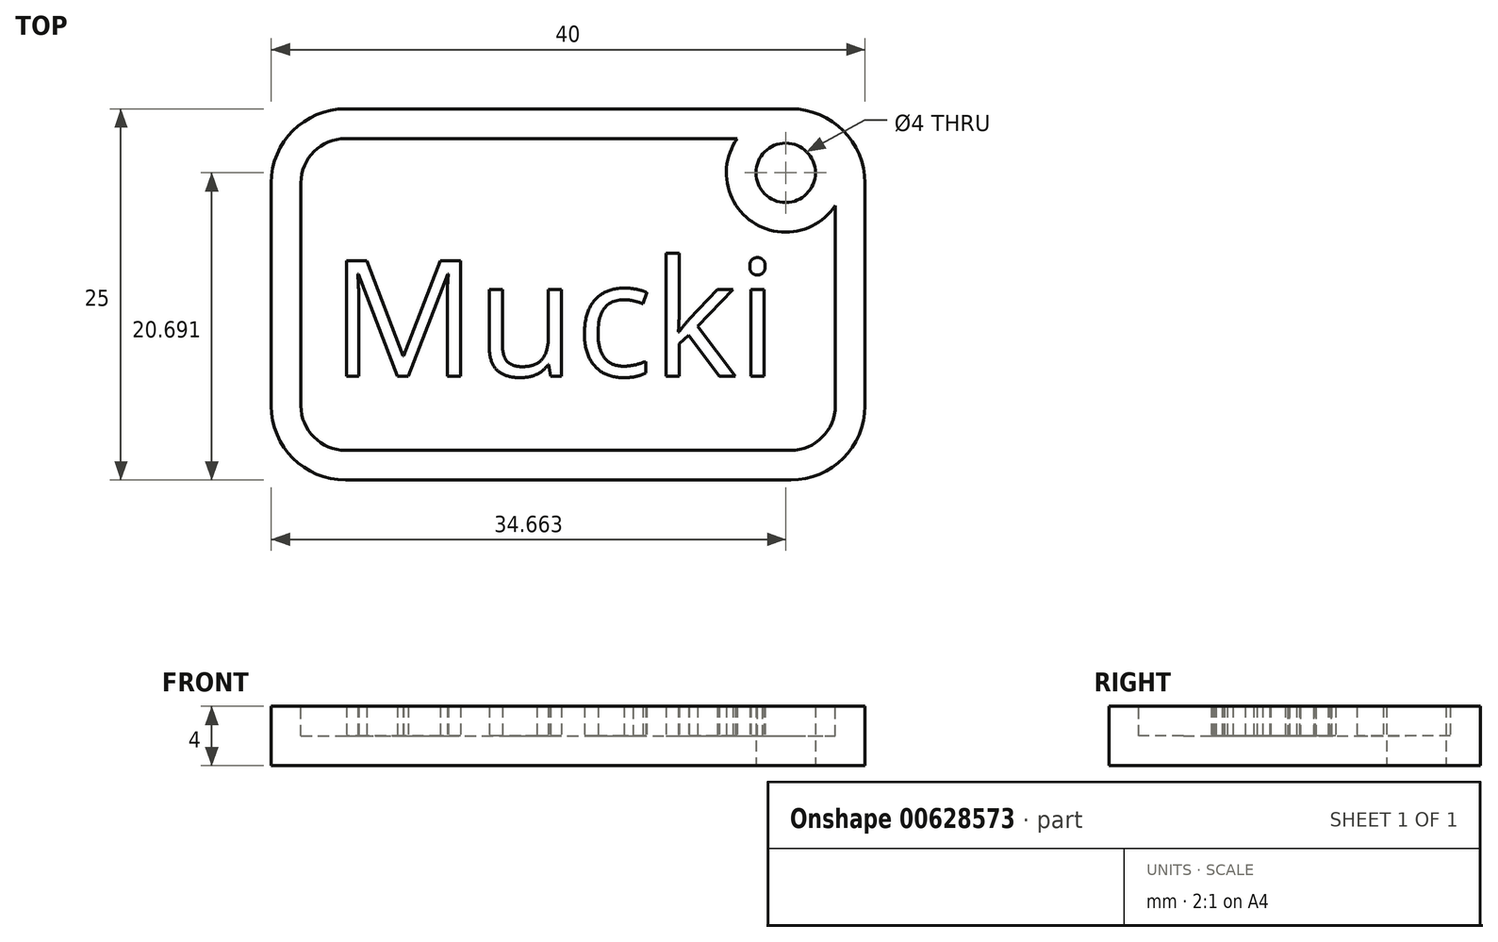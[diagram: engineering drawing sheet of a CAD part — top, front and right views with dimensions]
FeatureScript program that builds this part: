
annotation { "Feature Type Name" : "Feature", "Feature Type Description" : "" }
export const myFeature = defineFeature(function(context is Context, id is Id, definition is map)
    precondition{}
    {
        {
            var Q0;
            Q0=qCreatedBy(makeId("Top.planeOp"),FACE);
            var sketch = newSketch(context, id + "F0", { "sketchPlane" : qUnion([Q0])});
            skLineSegment(sketch, "E0.bottom", {"start": v(5, 0) * mm, "end": v(35, 0) * mm});
            skLineSegment(sketch, "E0.top", {"start": v(5, 25) * mm, "end": v(35, 25) * mm});
            skLineSegment(sketch, "E0.left", {"start": v(0, 5) * mm, "end": v(0, 20) * mm});
            skLineSegment(sketch, "E0.right", {"start": v(40, 5) * mm, "end": v(40, 20) * mm});
            skPoint(sketch, "E1.visualSharp", {"position": v(0, 25) * mm});
            skArc(sketch, "E1.filletArc", {"start": v(5, 25) * mm, "mid": v(1.46, 23.54) * mm, "end": v(0, 20) * mm});
            skPoint(sketch, "E2.visualSharp", {"position": v(0, 0) * mm});
            skArc(sketch, "E2.filletArc", {"start": v(0, 5) * mm, "mid": v(1.46, 1.46) * mm, "end": v(5, 0) * mm});
            skPoint(sketch, "E3.visualSharp", {"position": v(40, 0) * mm});
            skArc(sketch, "E3.filletArc", {"start": v(35, 0) * mm, "mid": v(38.54, 1.46) * mm, "end": v(40, 5) * mm});
            skPoint(sketch, "E4.visualSharp", {"position": v(40, 25) * mm});
            skArc(sketch, "E4.filletArc", {"start": v(40, 20) * mm, "mid": v(38.54, 23.54) * mm, "end": v(35, 25) * mm});
            skSolve(sketch);
        }
        {
            var Q0;
            Q0=qCreatedBy(makeId("Top.planeOp"),FACE);
            var sketch = newSketch(context, id + "F1", { "sketchPlane" : qUnion([Q0])});
            skPoint(sketch, "E5", {"position": v(34.66, 20.7) * mm});
            skSolve(sketch);
        }
        {
            var Q0;
            Q0 = qSketchRegion(id + "F0", true);
            extrude(context, id + "F2", {"entities" : qUnion([Q0]), "depth" : 4 * mm, "offsetDistance" : 25 * mm});
        }
        {
            var Q0;
            Q0=sQuery(id+"F1.wireOp",VERTEX,"E5");
            var Q1;
            Q1=makeQuery(id+"F2.opExtrude","SWEPT_BODY",BODY,{"disambiguationData":[OSD([sQuery(id+"F0.wireOp",EDGE,"E0.bottom"),sQuery(id+"F0.wireOp",EDGE,"E0.top"),sQuery(id+"F0.wireOp",EDGE,"E0.left"),sQuery(id+"F0.wireOp",EDGE,"E0.right"),sQuery(id+"F0.wireOp",EDGE,"E1.filletArc"),sQuery(id+"F0.wireOp",EDGE,"E2.filletArc"),sQuery(id+"F0.wireOp",EDGE,"E3.filletArc"),sQuery(id+"F0.wireOp",EDGE,"E4.filletArc")])]});
            hole(context, id + "F3", {"style" : HoleStyle.SIMPLE, "endStyle" : HoleEndStyle.THROUGH, "oppositeDirection" : true, "holeDiameter" : 4 * mm, "majorDiameter" : 5 * mm, "isTappedThrough" : true, "tappedDepth" : 12 * mm, "tapClearance" : 3, "locations" : qUnion([Q0]), "scope" : qUnion([Q1])});
        }
        {
            var Q0;
            Q0=makeQuery(id+"F2.opExtrude","CAP_FACE",FACE,{"disambiguationData":[OSD([sQuery(id+"F0.wireOp",EDGE,"E0.bottom"),sQuery(id+"F0.wireOp",EDGE,"E0.top"),sQuery(id+"F0.wireOp",EDGE,"E0.left"),sQuery(id+"F0.wireOp",EDGE,"E0.right"),sQuery(id+"F0.wireOp",EDGE,"E1.filletArc"),sQuery(id+"F0.wireOp",EDGE,"E2.filletArc"),sQuery(id+"F0.wireOp",EDGE,"E3.filletArc"),sQuery(id+"F0.wireOp",EDGE,"E4.filletArc")])],"isStart":false});
            shell(context, id + "F4", {"entities" : qUnion([Q0]), "thickness" : 2 * mm});
        }
        {
            var Q0;
            Q0=qCreatedBy(makeId("Top.planeOp"),FACE);
            var sketch = newSketch(context, id + "F5", { "sketchPlane" : qUnion([Q0])});
            skText(sketch, "E6", { "text": "Mucki", "fontName": "OpenSans-Regular.ttf"});
            const initialGuessF5  = {"E6": [0.004, 0.007, 1, 0, 0.00783]};
            skSetInitialGuess(sketch, initialGuessF5);
            skSolve(sketch);
        }
        {
            var Q0;
            Q0 = qSketchRegion(id + "F5", true);
            extrude(context, id + "F6", {"entities" : qUnion([Q0]), "operationType" : NewBodyOperationType.ADD, "depth" : 4 * mm, "offsetDistance" : 25 * mm});
        }
    });
